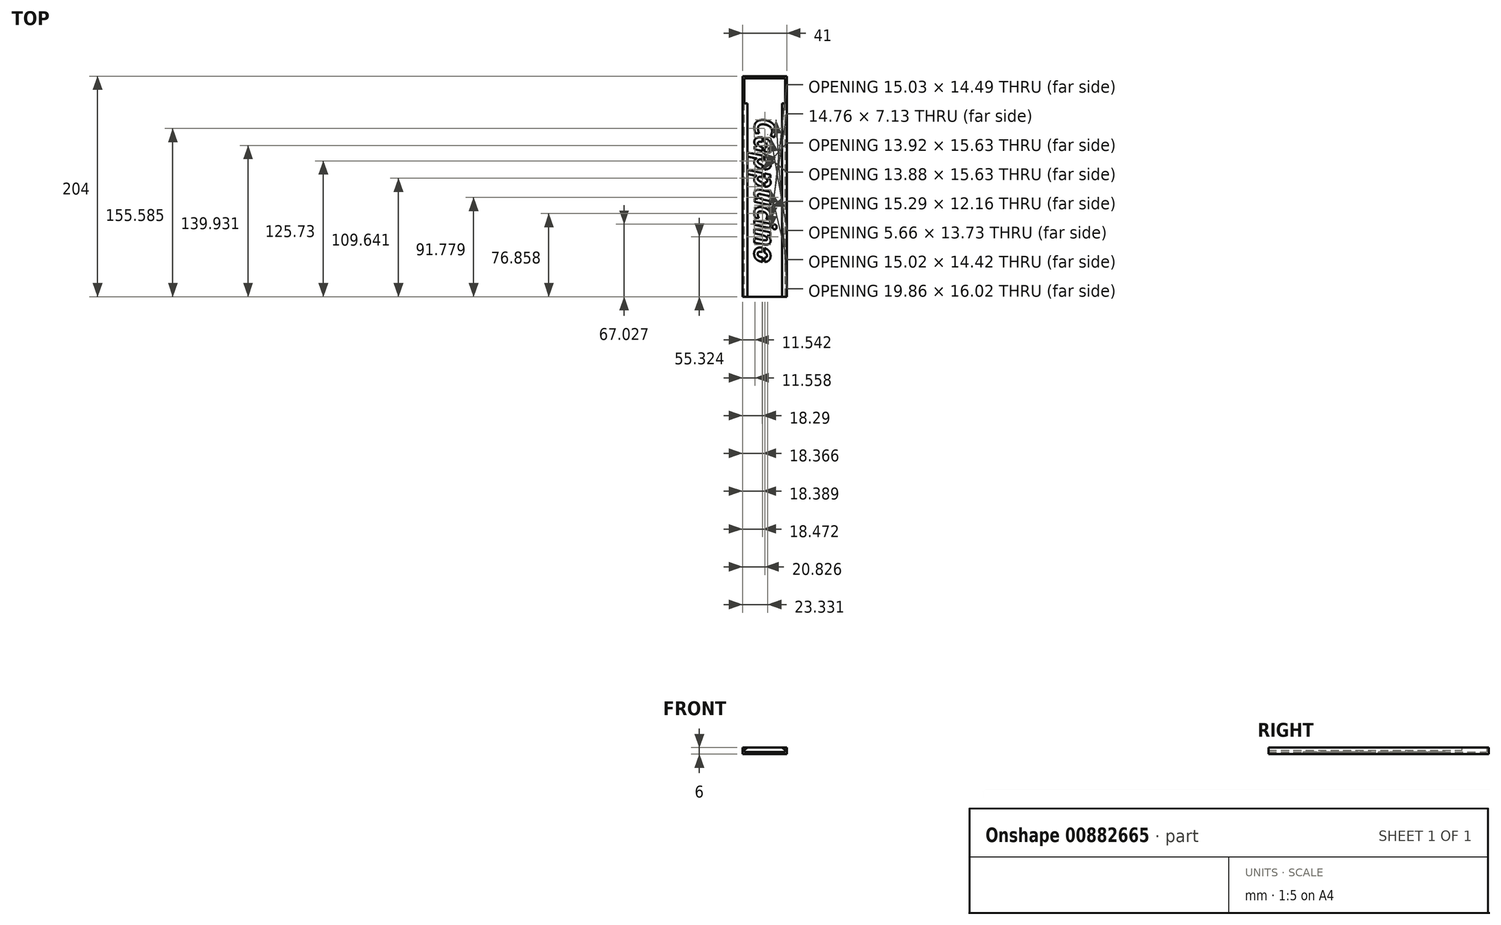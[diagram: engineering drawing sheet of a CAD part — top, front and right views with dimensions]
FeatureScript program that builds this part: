
annotation { "Feature Type Name" : "Feature", "Feature Type Description" : "" }
export const myFeature = defineFeature(function(context is Context, id is Id, definition is map)
    precondition{}
    {
        {
            var Q0;
            Q0=qCreatedBy(makeId("Front.planeOp"),FACE);
            var sketch = newSketch(context, id + "F0", { "sketchPlane" : qUnion([Q0])});
            skLineSegment(sketch, "E0", {"start": v(-20.5, 0) * mm, "end": v(20.5, 0) * mm});
            skLineSegment(sketch, "E1", {"start": v(20.5, 0) * mm, "end": v(20.5, 6) * mm});
            skLineSegment(sketch, "E2", {"start": v(20.5, 6) * mm, "end": v(16, 6) * mm});
            skLineSegment(sketch, "E3", {"start": v(19, 2) * mm, "end": v(-19, 2) * mm});
            skLineSegment(sketch, "E4", {"start": v(-16, 6) * mm, "end": v(-20.5, 6) * mm});
            skLineSegment(sketch, "E5", {"start": v(-20.5, 6) * mm, "end": v(-20.5, 0) * mm});
            skLineSegment(sketch, "E6", {"start": v(-16, 6) * mm, "end": v(16, 6) * mm});
            skLineSegment(sketch, "E7", {"start": v(16, 6) * mm, "end": v(19, 3.6) * mm});
            skLineSegment(sketch, "E8", {"start": v(19, 3.6) * mm, "end": v(19, 2) * mm});
            skLineSegment(sketch, "E9", {"start": v(-16, 6) * mm, "end": v(-19, 3.6) * mm});
            skLineSegment(sketch, "E10", {"start": v(-19, 3.6) * mm, "end": v(-19, 2) * mm});
            skSolve(sketch);
        }
        {
            var Q0;
            Q0=makeQuery(id+"F0.imprint","IMPRINT",FACE,{"disambiguationData":[TD([[makeQuery(id+"F0.imprint","IMPRINT",EDGE,{"derivedFrom":sQuery(id+"F0.wireOp",EDGE,"E0")}),1.0]])]});
            extrude(context, id + "F1", {"entities" : qUnion([Q0]), "depth" : 202 * mm, "offsetDistance" : 25 * mm});
        }
        {
            var Q0;
            Q0=qCreatedBy(makeId("Front.planeOp"),FACE);
            var sketch = newSketch(context, id + "F2", { "sketchPlane" : qUnion([Q0])});
            skLineSegment(sketch, "E11.bottom", {"start": v(20.5, 6) * mm, "end": v(-20.5, 6) * mm});
            skLineSegment(sketch, "E11.top", {"start": v(20.5, 0) * mm, "end": v(-20.5, 0) * mm});
            skLineSegment(sketch, "E11.left", {"start": v(20.5, 6) * mm, "end": v(20.5, 0) * mm});
            skLineSegment(sketch, "E11.right", {"start": v(-20.5, 6) * mm, "end": v(-20.5, 0) * mm});
            skSolve(sketch);
        }
        {
            var Q0;
            Q0=makeQuery(id+"F2.imprint","IMPRINT",FACE,{"disambiguationData":[TD([[makeQuery(id+"F2.imprint","IMPRINT",EDGE,{"derivedFrom":sQuery(id+"F2.wireOp",EDGE,"E11.bottom")}),1.0]])]});
            extrude(context, id + "F3", {"entities" : qUnion([Q0]), "operationType" : NewBodyOperationType.ADD, "oppositeDirection" : true, "depth" : 2 * mm, "offsetDistance" : 25 * mm});
        }
        {
            var Q0;
            Q0=makeQuery(id+"F3.boolean.opBoolean","MERGE",FACE,{"derivedFrom":[makeQuery(id+"F1.opExtrude","SWEPT_FACE",FACE,{"disambiguationData":[OSD([sQuery(id+"F0.wireOp",EDGE,"E2")])]}),makeQuery(id+"F1.opExtrude","SWEPT_FACE",FACE,{"disambiguationData":[OSD([sQuery(id+"F0.wireOp",EDGE,"E4")])]}),makeQuery(id+"F3.opExtrude","SWEPT_FACE",FACE,{"disambiguationData":[OSD([sQuery(id+"F2.wireOp",EDGE,"E11.bottom")])]})]});
            cPlane(context, id + "F4", {"entities" : qUnion([Q0]), "cplaneType" : CPlaneType.OFFSET, "offset" : 0 * mm, "width" : 150 * mm, "height" : 150 * mm});
        }
        {
            var Q0;
            Q0=qCreatedBy(id+"F4.planeOp",FACE);
            var sketch = newSketch(context, id + "F5", { "sketchPlane" : qUnion([Q0])});
            skLineSegment(sketch, "E12.bottom", {"start": v(19, 0) * mm, "end": v(-19, 0) * mm});
            skLineSegment(sketch, "E12.top", {"start": v(19, -23) * mm, "end": v(-19, -23) * mm});
            skLineSegment(sketch, "E12.left", {"start": v(19, 0) * mm, "end": v(19, -23) * mm});
            skLineSegment(sketch, "E12.right", {"start": v(-19, 0) * mm, "end": v(-19, -23) * mm});
            skSolve(sketch);
        }
        {
            var Q0;
            Q0=makeQuery(id+"F5.imprint","IMPRINT",FACE,{"disambiguationData":[TD([[makeQuery(id+"F5.imprint","IMPRINT",EDGE,{"derivedFrom":sQuery(id+"F5.wireOp",EDGE,"E12.bottom")}),1.0]])]});
            extrude(context, id + "F6", {"entities" : qUnion([Q0]), "operationType" : NewBodyOperationType.REMOVE, "oppositeDirection" : true, "depth" : 4 * mm, "offsetDistance" : 25 * mm});
        }
        {
            var Q0;
            Q0=qCreatedBy(id+"F4.planeOp",FACE);
            var sketch = newSketch(context, id + "F7", { "sketchPlane" : qUnion([Q0])});
            skText(sketch, "E13", { "text": "Cappucino", "fontName": "OpenSans-BoldItalic.ttf"});
            skLineSegment(sketch, "E14.bottom", {"start": v(0, -54.14) * mm, "end": v(-2, -54.14) * mm});
            skLineSegment(sketch, "E14.top", {"start": v(0, -170.87) * mm, "end": v(-2, -170.87) * mm});
            skLineSegment(sketch, "E14.left", {"start": v(0, -54.14) * mm, "end": v(0, -101.23) * mm});
            skLineSegment(sketch, "E14.right", {"start": v(-2, -54.14) * mm, "end": v(-2, -101.23) * mm});
            skLineSegment(sketch, "E15", {"start": v(0, -101.23) * mm, "end": v(-2, -101.23) * mm});
            skLineSegment(sketch, "E16", {"start": v(0, -155.49) * mm, "end": v(0, -155.49) * mm});
            skLineSegment(sketch, "E17", {"start": v(-2, -155.49) * mm, "end": v(-2, -170.87) * mm});
            skLineSegment(sketch, "E18", {"start": v(0, -155.49) * mm, "end": v(-2, -155.49) * mm});
            skLineSegment(sketch, "E19", {"start": v(0, -155.49) * mm, "end": v(0, -170.87) * mm});
            const initialGuessF7  = {"E13": [-0.00932, -0.03677, -0.00195, -1, 0.01946]};
            skSetInitialGuess(sketch, initialGuessF7);
            skSolve(sketch);
        }
        {
            var Q0;
            Q0=makeQuery(id+"F7.imprint","IMPRINT",FACE,{"disambiguationData":[TD([[makeQuery(id+"F7.imprint","IMPRINT",EDGE,{"derivedFrom":sQuery(id+"F7.wireOp",EDGE,"E13.sketch_text.stroke-93")}),-1.0]])]});
            var Q1;
            {var subQ4=sQuery(id+"F7.wireOp",EDGE,"E13.sketch_text.stroke-71");Q1=makeQuery(id+"F7.imprint","IMPRINT",FACE,{"disambiguationData":[TD([[makeQuery(id+"F7.imprint","IMPRINT",EDGE,{"derivedFrom":subQ4}),-1.0]])]});}
            var Q2;
            Q2=makeQuery(id+"F7.imprint","IMPRINT",FACE,{"disambiguationData":[TD([[makeQuery(id+"F7.imprint","IMPRINT",EDGE,{"derivedFrom":sQuery(id+"F7.wireOp",EDGE,"E13.sketch_text.stroke-68")}),-1.0]])]});
            var Q3;
            {var subQ8=sQuery(id+"F7.wireOp",EDGE,"E13.sketch_text.stroke-46");Q3=makeQuery(id+"F7.imprint","IMPRINT",FACE,{"disambiguationData":[TD([[makeQuery(id+"F7.imprint","IMPRINT",EDGE,{"derivedFrom":subQ8}),-1.0]])]});}
            var Q4;
            Q4=makeQuery(id+"F7.imprint","IMPRINT",FACE,{"disambiguationData":[TD([[makeQuery(id+"F7.imprint","IMPRINT",EDGE,{"derivedFrom":sQuery(id+"F7.wireOp",EDGE,"E13.sketch_text.stroke-43")}),-1.0]])]});
            var Q5;
            Q5=makeQuery(id+"F7.imprint","IMPRINT",FACE,{"disambiguationData":[TD([[makeQuery(id+"F7.imprint","IMPRINT",EDGE,{"derivedFrom":sQuery(id+"F7.wireOp",EDGE,"E13.sketch_text.stroke-18")}),-1.0]])]});
            var Q6;
            {var subQ7=sQuery(id+"F7.wireOp",EDGE,"E13.sketch_text.stroke-21");Q6=makeQuery(id+"F7.imprint","IMPRINT",FACE,{"disambiguationData":[TD([[makeQuery(id+"F7.imprint","IMPRINT",EDGE,{"derivedFrom":subQ7}),-1.0]])]});}
            var Q7;
            Q7=makeQuery(id+"F7.imprint","IMPRINT",FACE,{"disambiguationData":[TD([[makeQuery(id+"F7.imprint","IMPRINT",EDGE,{"derivedFrom":sQuery(id+"F7.wireOp",EDGE,"E13.sketch_text.stroke-0")}),-1.0]])]});
            var Q8;
            Q8=makeQuery(id+"F7.imprint","IMPRINT",FACE,{"disambiguationData":[TD([[makeQuery(id+"F7.imprint","IMPRINT",EDGE,{"derivedFrom":sQuery(id+"F7.wireOp",EDGE,"E13.sketch_text.stroke-110")}),-1.0]])]});
            var Q9;
            Q9=makeQuery(id+"F7.imprint","IMPRINT",FACE,{"disambiguationData":[TD([[makeQuery(id+"F7.imprint","IMPRINT",EDGE,{"derivedFrom":sQuery(id+"F7.wireOp",EDGE,"E13.sketch_text.stroke-135")}),-1.0]])]});
            var Q10;
            Q10=makeQuery(id+"F7.imprint","IMPRINT",FACE,{"disambiguationData":[TD([[makeQuery(id+"F7.imprint","IMPRINT",EDGE,{"derivedFrom":sQuery(id+"F7.wireOp",EDGE,"E13.sketch_text.stroke-128")}),-1.0]])]});
            var Q11;
            Q11=makeQuery(id+"F7.imprint","IMPRINT",FACE,{"disambiguationData":[TD([[makeQuery(id+"F7.imprint","IMPRINT",EDGE,{"derivedFrom":sQuery(id+"F7.wireOp",EDGE,"E13.sketch_text.stroke-139")}),-1.0]])]});
            var Q12;
            {var subQ12=sQuery(id+"F7.wireOp",EDGE,"E13.sketch_text.stroke-160");Q12=makeQuery(id+"F7.imprint","IMPRINT",FACE,{"disambiguationData":[TD([[makeQuery(id+"F7.imprint","IMPRINT",EDGE,{"derivedFrom":subQ12}),-1.0]])]});}
            var Q13;
            {var subQ9=sQuery(id+"F7.wireOp",EDGE,"E13.sketch_text.stroke-157");Q13=makeQuery(id+"F7.imprint","IMPRINT",FACE,{"disambiguationData":[TD([[makeQuery(id+"F7.imprint","IMPRINT",EDGE,{"derivedFrom":subQ9}),-1.0]])]});}
            extrude(context, id + "F8", {"entities" : qUnion([Q0, Q1, Q2, Q3, Q4, Q5, Q6, Q7, Q8, Q9, Q10, Q11, Q12, Q13]), "operationType" : NewBodyOperationType.REMOVE, "oppositeDirection" : true, "depth" : 11.2 * mm, "offsetDistance" : 25 * mm});
        }
    });
